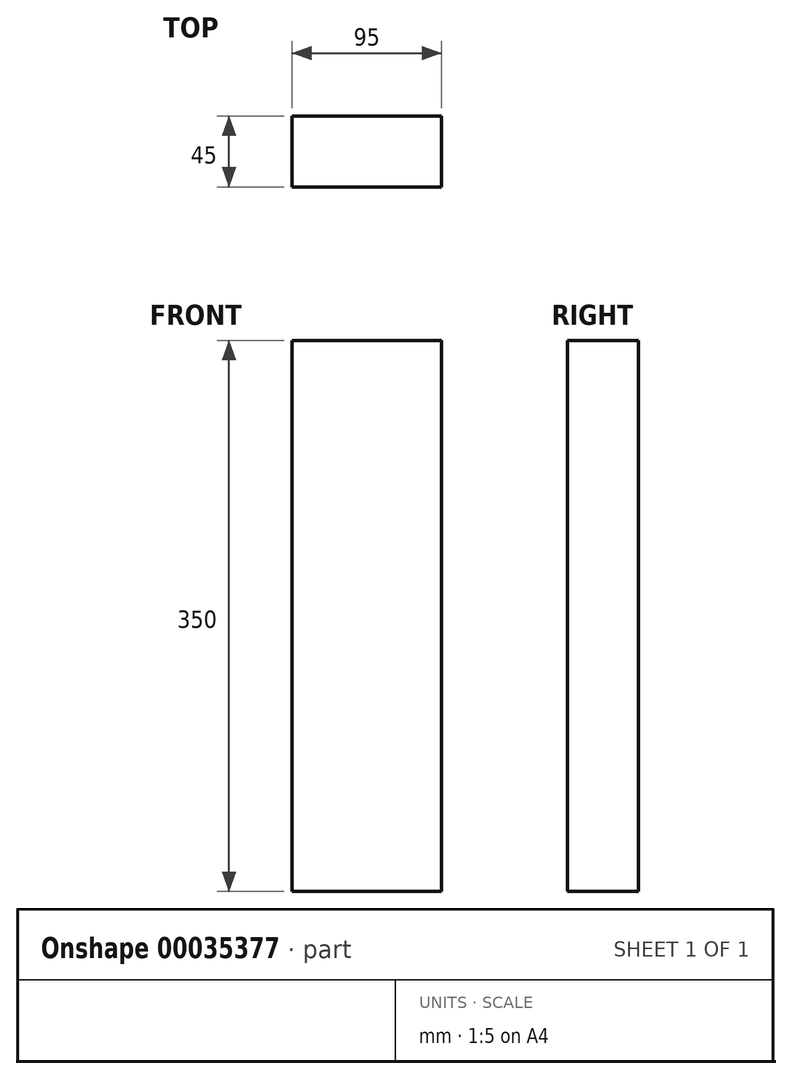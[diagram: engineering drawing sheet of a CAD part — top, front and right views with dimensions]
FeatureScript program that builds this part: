
annotation { "Feature Type Name" : "Feature", "Feature Type Description" : "" }
export const myFeature = defineFeature(function(context is Context, id is Id, definition is map)
    precondition{}
    {
        {
            var Q0;
            Q0=qCreatedBy(makeId("Top.planeOp"),FACE);
            var sketch = newSketch(context, id + "F0", { "sketchPlane" : qUnion([Q0])});
            skLineSegment(sketch, "E0.rect.bottom", {"start": v(47.5, -22.5) * mm, "end": v(-47.5, -22.5) * mm});
            skLineSegment(sketch, "E0.rect.top", {"start": v(47.5, 22.5) * mm, "end": v(-47.5, 22.5) * mm});
            skLineSegment(sketch, "E0.rect.left", {"start": v(47.5, -22.5) * mm, "end": v(47.5, 22.5) * mm});
            skLineSegment(sketch, "E0.rect.right", {"start": v(-47.5, -22.5) * mm, "end": v(-47.5, 22.5) * mm});
            skPoint(sketch, "E0.rect.middle", {"position": v(0, 0) * mm});
            skSolve(sketch);
        }
        {
            var Q0;
            Q0=makeQuery(id+"F0.imprint","IMPRINT",FACE,{"disambiguationData":[TD([[makeQuery(id+"F0.imprint","IMPRINT",EDGE,{"derivedFrom":sQuery(id+"F0.wireOp",EDGE,"E0.rect.bottom")}),-1.0]])]});
            extrude(context, id + "F1", {"entities" : qUnion([Q0]), "depth" : 350 * mm});
        }
    });
